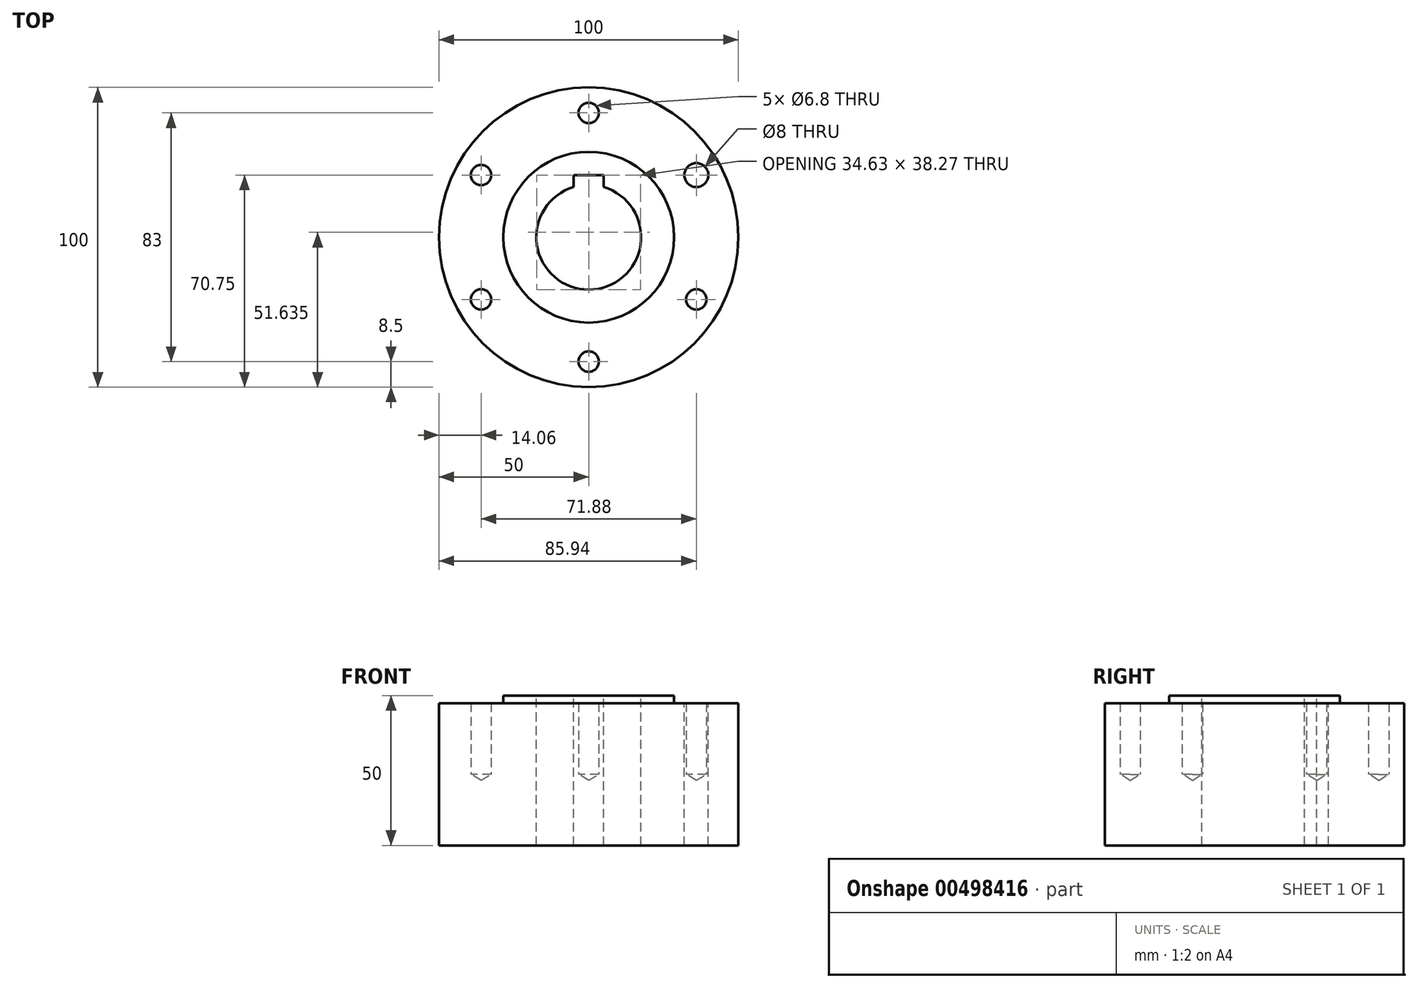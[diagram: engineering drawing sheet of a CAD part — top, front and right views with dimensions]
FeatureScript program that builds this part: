
annotation { "Feature Type Name" : "Feature", "Feature Type Description" : "" }
export const myFeature = defineFeature(function(context is Context, id is Id, definition is map)
    precondition{}
    {
        {
            var Q0;
            Q0=qCreatedBy(makeId("Top.planeOp"),FACE);
            var sketch = newSketch(context, id + "F0", { "sketchPlane" : qUnion([Q0])});
            skArc(sketch, "E0", {"start": v(-5, 16.77) * mm, "mid": v(0, -17.5) * mm, "end": v(5, 16.77) * mm});
            skCircle(sketch, "E1", {"center": v(0, 0) * mm, "radius": 28.5 * mm});
            skCircle(sketch, "E2", {"center": v(0, 0) * mm, "radius": 50 * mm});
            skCircle(sketch, "E3", {"center": v(0, 0) * mm, "radius": 41.5 * mm});
            skCircle(sketch, "E4", {"center": v(0, 41.5) * mm, "radius": 4 * mm});
            skCircle(sketch, "E5.1.0", {"center": v(-35.94, 20.75) * mm, "radius": 4 * mm});
            skCircle(sketch, "E5.2.0", {"center": v(-35.94, -20.75) * mm, "radius": 4 * mm});
            skCircle(sketch, "E5.3.0", {"center": v(0, -41.5) * mm, "radius": 4 * mm});
            skCircle(sketch, "E5.4.0", {"center": v(35.94, -20.75) * mm, "radius": 4 * mm});
            skCircle(sketch, "E5.5.0", {"center": v(35.94, 20.75) * mm, "radius": 4 * mm});
            skLineSegment(sketch, "E6.bottom", {"start": v(-5, 20.77) * mm, "end": v(5, 20.77) * mm});
            skLineSegment(sketch, "E6.left", {"start": v(-5, 20.77) * mm, "end": v(-5, 16.77) * mm});
            skLineSegment(sketch, "E6.right", {"start": v(5, 20.77) * mm, "end": v(5, 16.77) * mm});
            skSolve(sketch);
        }
        {
            var Q0;
            Q0=makeQuery(id+"F0.imprint","IMPRINT",FACE,{"disambiguationData":[TD([[makeQuery(id+"F0.imprint","IMPRINT",EDGE,{"derivedFrom":sQuery(id+"F0.wireOp",EDGE,"E1")}),-1.0]])]});
            var Q1;
            Q1=makeQuery(id+"F0.imprint","IMPRINT",FACE,{"disambiguationData":[TD([[makeQuery(id+"F0.imprint","IMPRINT",EDGE,{"derivedFrom":sQuery(id+"F0.wireOp",EDGE,"E2")}),1.0]])]});
            var Q2;
            {var subQ0=sQuery(id+"F0.wireOp",EDGE,"E3");var subQ1=sQuery(id+"F0.wireOp",EDGE,"E5.1.0");var subQ2=makeQuery(id+"F0.imprint","INTERSECT",VERTEX,{"disambiguationData":[OD(0.0)],"derivedFrom":[subQ1,subQ0]});Q2=makeQuery(id+"F0.imprint","IMPRINT",FACE,{"disambiguationData":[TD([[makeQuery(id+"F0.imprint","IMPRINT",EDGE,{"disambiguationData":[TD([[subQ2,1.0]])],"derivedFrom":subQ1}),1.0]])]});}
            var Q3;
            {var subQ0=sQuery(id+"F0.wireOp",EDGE,"E3");var subQ1=sQuery(id+"F0.wireOp",EDGE,"E5.1.0");var subQ2=makeQuery(id+"F0.imprint","INTERSECT",VERTEX,{"disambiguationData":[OD(0.0)],"derivedFrom":[subQ1,subQ0]});Q3=makeQuery(id+"F0.imprint","IMPRINT",FACE,{"disambiguationData":[TD([[makeQuery(id+"F0.imprint","IMPRINT",EDGE,{"disambiguationData":[TD([[subQ2,-1.0]])],"derivedFrom":subQ1}),1.0]])]});}
            var Q4;
            {var subQ0=sQuery(id+"F0.wireOp",EDGE,"E3");var subQ1=sQuery(id+"F0.wireOp",EDGE,"E5.2.0");var subQ2=makeQuery(id+"F0.imprint","INTERSECT",VERTEX,{"disambiguationData":[OD(0.0)],"derivedFrom":[subQ1,subQ0]});Q4=makeQuery(id+"F0.imprint","IMPRINT",FACE,{"disambiguationData":[TD([[makeQuery(id+"F0.imprint","IMPRINT",EDGE,{"disambiguationData":[TD([[subQ2,1.0]])],"derivedFrom":subQ1}),1.0]])]});}
            var Q5;
            {var subQ0=sQuery(id+"F0.wireOp",EDGE,"E3");var subQ1=sQuery(id+"F0.wireOp",EDGE,"E5.2.0");var subQ2=makeQuery(id+"F0.imprint","INTERSECT",VERTEX,{"disambiguationData":[OD(0.0)],"derivedFrom":[subQ1,subQ0]});Q5=makeQuery(id+"F0.imprint","IMPRINT",FACE,{"disambiguationData":[TD([[makeQuery(id+"F0.imprint","IMPRINT",EDGE,{"disambiguationData":[TD([[subQ2,-1.0]])],"derivedFrom":subQ1}),1.0]])]});}
            var Q6;
            {var subQ0=sQuery(id+"F0.wireOp",EDGE,"E5.3.0");var subQ1=sQuery(id+"F0.wireOp",EDGE,"E3");var subQ2=makeQuery(id+"F0.imprint","INTERSECT",VERTEX,{"disambiguationData":[OD(0.0)],"derivedFrom":[subQ1,subQ0]});Q6=makeQuery(id+"F0.imprint","IMPRINT",FACE,{"disambiguationData":[TD([[makeQuery(id+"F0.imprint","IMPRINT",EDGE,{"disambiguationData":[TD([[subQ2,-1.0]])],"derivedFrom":subQ1}),1.0]])]});}
            var Q7;
            {var subQ0=sQuery(id+"F0.wireOp",EDGE,"E5.3.0");var subQ1=sQuery(id+"F0.wireOp",EDGE,"E3");var subQ2=makeQuery(id+"F0.imprint","INTERSECT",VERTEX,{"disambiguationData":[OD(0.0)],"derivedFrom":[subQ1,subQ0]});Q7=makeQuery(id+"F0.imprint","IMPRINT",FACE,{"disambiguationData":[TD([[makeQuery(id+"F0.imprint","IMPRINT",EDGE,{"disambiguationData":[TD([[subQ2,-1.0]])],"derivedFrom":subQ1}),-1.0]])]});}
            var Q8;
            {var subQ0=sQuery(id+"F0.wireOp",EDGE,"E5.4.0");var subQ1=sQuery(id+"F0.wireOp",EDGE,"E3");var subQ2=makeQuery(id+"F0.imprint","INTERSECT",VERTEX,{"disambiguationData":[OD(0.0)],"derivedFrom":[subQ1,subQ0]});Q8=makeQuery(id+"F0.imprint","IMPRINT",FACE,{"disambiguationData":[TD([[makeQuery(id+"F0.imprint","IMPRINT",EDGE,{"disambiguationData":[TD([[subQ2,-1.0]])],"derivedFrom":subQ1}),-1.0]])]});}
            var Q9;
            {var subQ0=sQuery(id+"F0.wireOp",EDGE,"E5.4.0");var subQ1=sQuery(id+"F0.wireOp",EDGE,"E3");var subQ2=makeQuery(id+"F0.imprint","INTERSECT",VERTEX,{"disambiguationData":[OD(0.0)],"derivedFrom":[subQ1,subQ0]});Q9=makeQuery(id+"F0.imprint","IMPRINT",FACE,{"disambiguationData":[TD([[makeQuery(id+"F0.imprint","IMPRINT",EDGE,{"disambiguationData":[TD([[subQ2,-1.0]])],"derivedFrom":subQ1}),1.0]])]});}
            var Q10;
            {var subQ0=sQuery(id+"F0.wireOp",EDGE,"E5.5.0");var subQ1=sQuery(id+"F0.wireOp",EDGE,"E3");var subQ2=makeQuery(id+"F0.imprint","INTERSECT",VERTEX,{"disambiguationData":[OD(0.0)],"derivedFrom":[subQ1,subQ0]});Q10=makeQuery(id+"F0.imprint","IMPRINT",FACE,{"disambiguationData":[TD([[makeQuery(id+"F0.imprint","IMPRINT",EDGE,{"disambiguationData":[TD([[subQ2,-1.0]])],"derivedFrom":subQ1}),1.0]])]});}
            var Q11;
            {var subQ0=sQuery(id+"F0.wireOp",EDGE,"E5.5.0");var subQ1=sQuery(id+"F0.wireOp",EDGE,"E3");var subQ2=makeQuery(id+"F0.imprint","INTERSECT",VERTEX,{"disambiguationData":[OD(0.0)],"derivedFrom":[subQ1,subQ0]});Q11=makeQuery(id+"F0.imprint","IMPRINT",FACE,{"disambiguationData":[TD([[makeQuery(id+"F0.imprint","IMPRINT",EDGE,{"disambiguationData":[TD([[subQ2,-1.0]])],"derivedFrom":subQ1}),-1.0]])]});}
            var Q12;
            {var subQ0=sQuery(id+"F0.wireOp",EDGE,"E3");var subQ1=sQuery(id+"F0.wireOp",EDGE,"E4");var subQ2=makeQuery(id+"F0.imprint","INTERSECT",VERTEX,{"disambiguationData":[OD(0.0)],"derivedFrom":[subQ1,subQ0]});Q12=makeQuery(id+"F0.imprint","IMPRINT",FACE,{"disambiguationData":[TD([[makeQuery(id+"F0.imprint","IMPRINT",EDGE,{"disambiguationData":[TD([[subQ2,-1.0]])],"derivedFrom":subQ1}),1.0]])]});}
            var Q13;
            {var subQ0=sQuery(id+"F0.wireOp",EDGE,"E3");var subQ1=sQuery(id+"F0.wireOp",EDGE,"E4");var subQ2=makeQuery(id+"F0.imprint","INTERSECT",VERTEX,{"disambiguationData":[OD(0.0)],"derivedFrom":[subQ1,subQ0]});Q13=makeQuery(id+"F0.imprint","IMPRINT",FACE,{"disambiguationData":[TD([[makeQuery(id+"F0.imprint","IMPRINT",EDGE,{"disambiguationData":[TD([[subQ2,1.0]])],"derivedFrom":subQ1}),1.0]])]});}
            extrude(context, id + "F1", {"entities" : qUnion([Q0, Q1, Q2, Q3, Q4, Q5, Q6, Q7, Q8, Q9, Q10, Q11, Q12, Q13]), "oppositeDirection" : true, "depth" : 47.5 * mm});
        }
        {
            var Q0;
            Q0=makeQuery(id+"F0.imprint","IMPRINT",FACE,{"disambiguationData":[TD([[makeQuery(id+"F0.imprint","IMPRINT",EDGE,{"derivedFrom":sQuery(id+"F0.wireOp",EDGE,"E0")}),-1.0]])]});
            extrude(context, id + "F2", {"entities" : qUnion([Q0]), "operationType" : NewBodyOperationType.ADD, "oppositeDirection" : true, "depth" : 47.5 * mm});
        }
        {
            var Q0;
            Q0=sQuery(id+"F0.wireOp",VERTEX,"E5.4.0.center");
            var Q1;
            Q1=sQuery(id+"F0.wireOp",VERTEX,"E5.5.0.center");
            var Q2;
            Q2=sQuery(id+"F0.wireOp",VERTEX,"E4.center");
            var Q3;
            Q3=sQuery(id+"F0.wireOp",VERTEX,"E5.1.0.center");
            var Q4;
            Q4=sQuery(id+"F0.wireOp",VERTEX,"E5.2.0.center");
            var Q5;
            Q5=sQuery(id+"F0.wireOp",VERTEX,"E5.3.0.center");
            var Q6;
            Q6=makeQuery(id+"F1.opExtrude","SWEPT_BODY",BODY,{"disambiguationData":[OSD([sQuery(id+"F0.wireOp",EDGE,"E1"),sQuery(id+"F0.wireOp",EDGE,"E2")])]});
            hole(context, id + "F3", {"style" : HoleStyle.C_BORE, "endStyle" : HoleEndStyle.BLIND, "holeDiameter" : 6.8 * mm, "cBoreDiameter" : 6.8 * mm, "cBoreDepth" : 1 * mm, "holeDepth" : 23.75 * mm, "isTappedThrough" : true, "tappedDepth" : 20 * mm, "tapClearance" : 3, "startFromSketch" : true, "locations" : qUnion([Q0, Q1, Q2, Q3, Q4, Q5]), "scope" : qUnion([Q6])});
        }
        {
            var Q0;
            Q0=makeQuery(id+"F0.imprint","IMPRINT",FACE,{"disambiguationData":[TD([[makeQuery(id+"F0.imprint","IMPRINT",EDGE,{"derivedFrom":sQuery(id+"F0.wireOp",EDGE,"E0")}),-1.0]])]});
            extrude(context, id + "F4", {"entities" : qUnion([Q0]), "operationType" : NewBodyOperationType.ADD, "depth" : 2.5 * mm});
        }
    });
